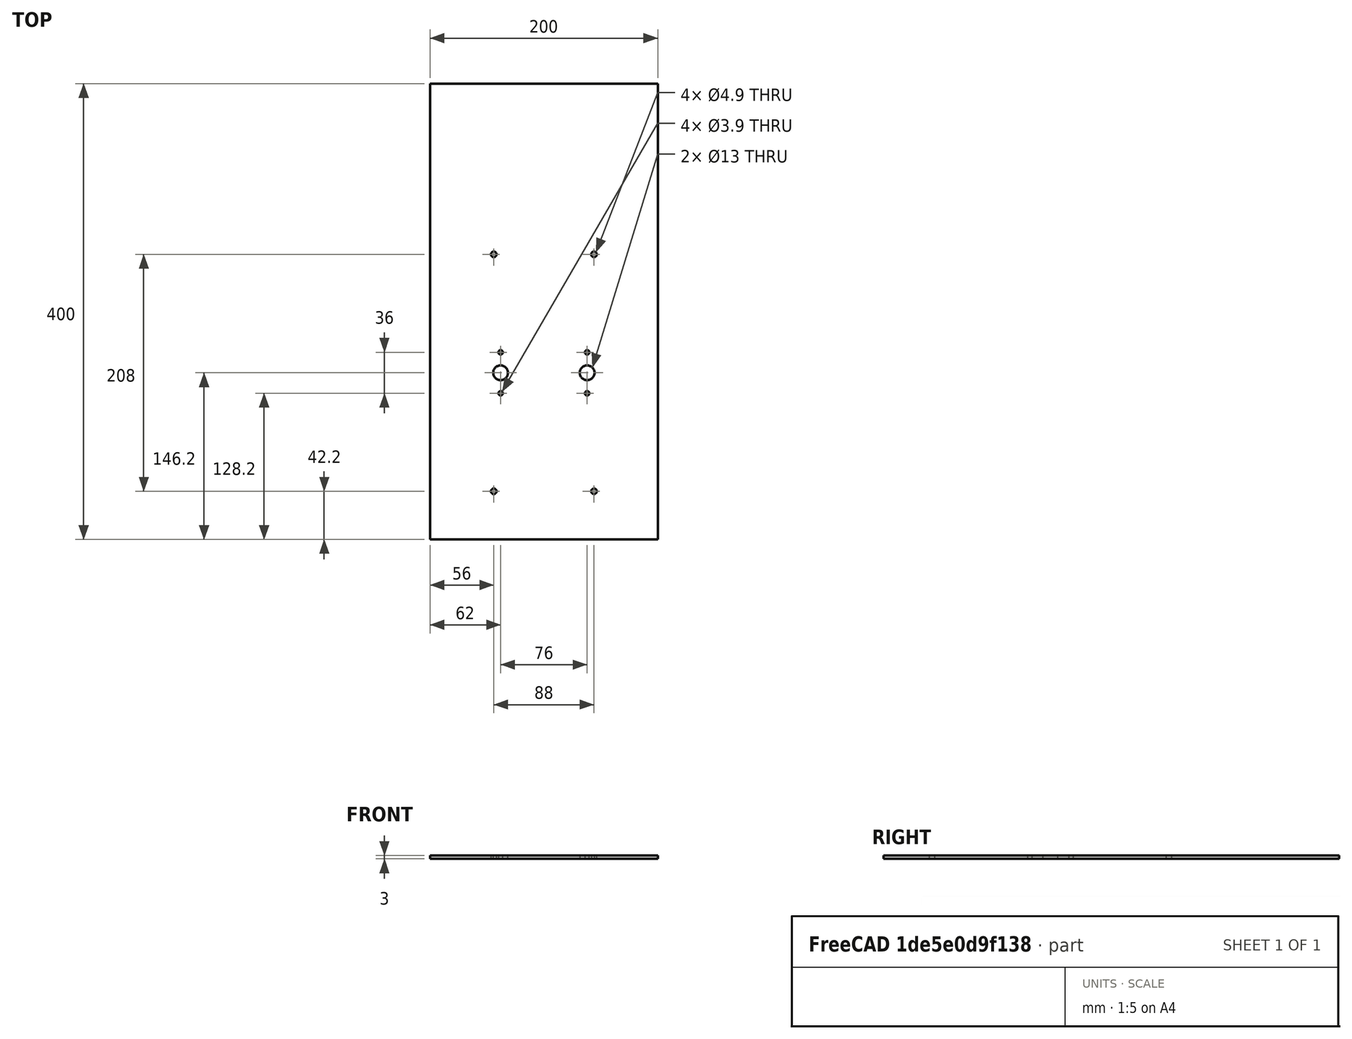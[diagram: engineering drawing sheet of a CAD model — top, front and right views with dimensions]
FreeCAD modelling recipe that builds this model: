
FCSTD DOCUMENT  (FreeCAD 1.0R38641 +468 (Git))
Label: plate_roof
License: All rights reserved
LicenseURL: https://en.wikipedia.org/wiki/All_rights_reserved
objects: TechDraw::DrawViewDimension×10, TechDraw::DrawProjGroupItem×2, Sketcher::SketchObject×1, PartDesign::Pad×1, PartDesign::Body×1, TechDraw::DrawSVGTemplate×1, TechDraw::DrawProjGroup×1, TechDraw::DrawPage×1
note: 22 computed .brp shape members not serialized (recipe doc carries the construction recipe); baked Part::Feature solids carry a one-line shape summary decoded from their .brp

FEATURE [Sketcher::SketchObject] Sketch
  ArcFitTolerance = 1e-06
  AttachmentSupport = -> [XY_Plane]
  FullyConstrained = false
  MakeInternals = false
  MapMode = 5
  sketch-geometry (16):
    g0: LineSegment StartX=-100 StartY=200 StartZ=0 EndX=-100 EndY=-200 EndZ=0
    g1: LineSegment StartX=-100 StartY=-200 StartZ=0 EndX=100 EndY=-200 EndZ=0
    g2: LineSegment StartX=100 StartY=-200 StartZ=0 EndX=100 EndY=200 EndZ=0
    g3: LineSegment StartX=100 StartY=200 StartZ=0 EndX=-100 EndY=200 EndZ=0
    g4: Circle CenterX=-44 CenterY=50.2 CenterZ=0 NormalX=0 NormalY=0 NormalZ=1 AngleXU=0 Radius=2.45
    g5: Circle CenterX=-44 CenterY=-157.8 CenterZ=0 NormalX=0 NormalY=0 NormalZ=1 AngleXU=0 Radius=2.45
    g6: Circle CenterX=44 CenterY=50.2 CenterZ=0 NormalX=0 NormalY=0 NormalZ=1 AngleXU=0 Radius=2.45
    g7: Circle CenterX=44 CenterY=-157.8 CenterZ=0 NormalX=0 NormalY=0 NormalZ=1 AngleXU=0 Radius=2.45
    g8: Circle [constr] CenterX=0 CenterY=0 CenterZ=0 NormalX=0 NormalY=0 NormalZ=1 AngleXU=0 Radius=9.44112
    g9: Circle CenterX=-38 CenterY=-35.8 CenterZ=0 NormalX=0 NormalY=0 NormalZ=1 AngleXU=0 Radius=1.95
    g10: Circle CenterX=-38 CenterY=-71.8 CenterZ=0 NormalX=0 NormalY=0 NormalZ=1 AngleXU=0 Radius=1.95
    g11: Circle CenterX=-38 CenterY=-53.8 CenterZ=0 NormalX=0 NormalY=0 NormalZ=1 AngleXU=0 Radius=6.5
    g12: Circle CenterX=38 CenterY=-35.8 CenterZ=0 NormalX=0 NormalY=0 NormalZ=1 AngleXU=0 Radius=1.95
    g13: Circle CenterX=38 CenterY=-53.8 CenterZ=0 NormalX=0 NormalY=0 NormalZ=1 AngleXU=0 Radius=6.5
    g14: Circle CenterX=38 CenterY=-71.8 CenterZ=0 NormalX=0 NormalY=0 NormalZ=1 AngleXU=0 Radius=1.95
    g15: LineSegment [constr] StartX=0 StartY=0 StartZ=0 EndX=0 EndY=174.663 EndZ=0
  constraints (44):
    c: Coincident(g0,g1)
    c: Coincident(g1,g2)
    c: Coincident(g2,g3)
    c: Coincident(g3,g0)
    c: Vertical(g0)
    c: Vertical(g2)
    c: Horizontal(g1)
    c: Horizontal(g3)
    c: DistanceY(g0,g0) = 400
    c: DistanceX(g3,g3) = 200
    c: Vertical(g4,g5)
    c: Diameter(g4) = 4.9
    c: Equal(g4,g5)
    c: DistanceY(g5,g4) = 208
    c: Horizontal(g6,g4)
    c: Horizontal(g7,g5)
    c: Equal(g6,g4)
    c: Equal(g4,g7)
    c: DistanceX(g4,g6) = 88
    c: Vertical(g7,g6)
    c: DistanceY(g8,g4) = 50.2
    c: DistanceX(g4,g8) = 44
    c: Distance(g8,g3) = 200
    c: Distance(g8,g0) = 100
    c: Vertical(g9,g11)
    c: Vertical(g11,g10)
    c: Vertical(g12,g13)
    c: Vertical(g13,g14)
    c: DistanceY(g11,g9) = 18
    c: DistanceY(g10,g11) = 18
    c: Diameter(g9) = 3.9
    c: Equal(g9,g10)
    c: Equal(g10,g12)
    c: Equal(g12,g14)
    c: Horizontal(g9,g12)
    c: Horizontal(g10,g14)
    c: Equal(g11,g13)
    c: Diameter(g11) = 13
    c: DistanceX(g11,g8) = 38
    c: Horizontal(g11,g13)
    c: DistanceY(g11,g4) = 104
    c: Coincident(g15,g8)
    c: Symmetric(g11,g13,g15)
    c: Coincident(g8,g-1)
FEATURE [PartDesign::Pad] Pad
  Direction = (0,0,1)
  Length = 3
  Length2 = 10
  Profile = -> Sketch
  ReferenceAxis = -> Sketch [N_Axis]
  Refine = true
  Suppressed = false
  Type = 0
FEATURE [PartDesign::Body] Body  label="plate_roof"
  AllowCompound = false
  Group = -> [Sketch,Pad]
  Origin = -> Origin
  Tip = -> Pad
FEATURE [TechDraw::DrawSVGTemplate] Template
  EditableTexts = approval_person=B. Hecate; creator=Djordje Vujic; date_of_issue=20.1.25.; document_type=Assembly Drawing; general_tolerances=ISO 2768-m; identification_number=DN; language_code=EN; part_material=Stainless steel Mat.No. 1.4301; revision_index=AAA; sheet_number=1 / 3; sheet_scale=1 : 2; title=plate_roof
  Height = 297
  Orientation = 0
  Template = /snap/freecad/1248/usr/share/Mod/TechDraw/Templates/A4_Portrait_ISO5457_minimal.svg
  Width = 210
FEATURE [TechDraw::DrawProjGroupItem] ProjItem  label="Front"
  CoarseView = false
  Direction = (0,0,1)
  Focus = 100
  HardHidden = false
  IsoCount = 0
  IsoHidden = false
  IsoVisible = false
  LockPosition = true
  Perspective = false
  Rotation = 0
  RotationVector = (1,0,0)
  Scale = 0.5
  ScaleType = 0
  ScrubCount = 1
  SeamHidden = false
  SeamVisible = false
  SmoothHidden = false
  SmoothVisible = true
  Source = -> [Body]
  Type = 0
  X = 0
  XDirection = (1,0,0)
  Y = 0
FEATURE [TechDraw::DrawProjGroupItem] ProjItem001  label="Bottom"
  CoarseView = false
  Direction = (0,-1,0)
  Focus = 100
  HardHidden = false
  IsoCount = 0
  IsoHidden = false
  IsoVisible = false
  LockPosition = false
  Perspective = false
  Rotation = 0
  RotationVector = (1,0,0)
  Scale = 0.5
  ScaleType = 0
  ScrubCount = 1
  SeamHidden = false
  SeamVisible = false
  SmoothHidden = false
  SmoothVisible = true
  Source = -> [Body]
  Type = 5
  X = 0
  XDirection = (1,0,0)
  Y = 115.75
FEATURE [TechDraw::DrawProjGroup] ProjGroup
  Anchor = -> ProjItem
  AutoDistribute = true
  LockPosition = false
  ProjectionType = 0
  Rotation = 0
  Scale = 0.5
  ScaleType = 2
  Source = -> [Body]
  Views = -> [ProjItem,ProjItem001]
  X = 105
  Y = 162.983
  spacingX = 15
  spacingY = 15
FEATURE [TechDraw::DrawViewDimension] Dimension
  AngleOverride = false
  Arbitrary = false
  ArbitraryTolerances = false
  BoxCorners = (2) [(-50,-0.75,0),(50,0.75,0)]
  EqualTolerance = true
  ExtensionAngle = 0
  FormatSpec = %.2w
  FormatSpecOverTolerance = %+.2w
  FormatSpecUnderTolerance = %+.2w
  Inverted = false
  LineAngle = 0
  LockPosition = false
  MeasureType = 1
  OverTolerance = 0
  References2D = -> [ProjItem001]
  Rotation = 0
  ScaleType = 0
  TheoreticalExact = false
  Type = 2
  UnderTolerance = 0
  X = -62.2509
  Y = -6.95305
FEATURE [TechDraw::DrawViewDimension] Dimension001
  AngleOverride = false
  Arbitrary = false
  ArbitraryTolerances = false
  BoxCorners = (2) [(-50,-0.75,0),(50,0.75,0)]
  EqualTolerance = true
  ExtensionAngle = 0
  FormatSpec = %.2w
  FormatSpecOverTolerance = %+.2w
  FormatSpecUnderTolerance = %+.2w
  Inverted = false
  LineAngle = 0
  LockPosition = false
  MeasureType = 1
  OverTolerance = 0
  References2D = -> [ProjItem001]
  Rotation = 0
  ScaleType = 0
  TheoreticalExact = false
  Type = 1
  UnderTolerance = 0
  X = 0
  Y = -5.41651
FEATURE [TechDraw::DrawViewDimension] Dimension002
  AngleOverride = false
  Arbitrary = false
  ArbitraryTolerances = false
  BoxCorners = (2) [(-50,-100,0),(50,100,0)]
  EqualTolerance = true
  ExtensionAngle = 0
  FormatSpec = %.2w
  FormatSpecOverTolerance = %+.2w
  FormatSpecUnderTolerance = %+.2w
  Inverted = false
  LineAngle = 0
  LockPosition = false
  MeasureType = 1
  OverTolerance = 0
  References2D = -> [ProjItem]
  Rotation = 0
  ScaleType = 0
  TheoreticalExact = false
  Type = 2
  UnderTolerance = 0
  X = -64.6458
  Y = 3.29053
FEATURE [TechDraw::DrawViewDimension] Dimension003
  AngleOverride = false
  Arbitrary = false
  ArbitraryTolerances = false
  BoxCorners = (2) [(-50,-100,0),(50,100,0)]
  EqualTolerance = true
  ExtensionAngle = 0
  FormatSpec = %.2w
  FormatSpecOverTolerance = %+.2w
  FormatSpecUnderTolerance = %+.2w
  Inverted = false
  LineAngle = 0
  LockPosition = false
  MeasureType = 1
  OverTolerance = 0
  References2D = -> [ProjItem]
  Rotation = 0
  ScaleType = 0
  TheoreticalExact = false
  Type = 0
  UnderTolerance = 0
  X = 29.0917
  Y = -31.4
FEATURE [TechDraw::DrawViewDimension] Dimension004
  AngleOverride = false
  Arbitrary = false
  ArbitraryTolerances = false
  BoxCorners = (2) [(-50,-100,0),(50,100,0)]
  EqualTolerance = true
  ExtensionAngle = 0
  FormatSpec = %.2w
  FormatSpecOverTolerance = %+.2w
  FormatSpecUnderTolerance = %+.2w
  Inverted = false
  LineAngle = 0
  LockPosition = false
  MeasureType = 1
  OverTolerance = 0
  References2D = -> [ProjItem]
  Rotation = 0
  ScaleType = 0
  TheoreticalExact = false
  Type = 0
  UnderTolerance = 0
  X = 0
  Y = -5.52183
FEATURE [TechDraw::DrawViewDimension] Dimension005
  AngleOverride = false
  Arbitrary = false
  ArbitraryTolerances = false
  BoxCorners = (2) [(-50,-100,0),(50,100,0)]
  EqualTolerance = true
  ExtensionAngle = 0
  FormatSpec = %.2w
  FormatSpecOverTolerance = %+.2w
  FormatSpecUnderTolerance = %+.2w
  Inverted = false
  LineAngle = 0
  LockPosition = false
  MeasureType = 1
  OverTolerance = 0
  References2D = -> [ProjItem]
  Rotation = 0
  ScaleType = 0
  TheoreticalExact = false
  Type = 0
  UnderTolerance = 0
  X = -34.5
  Y = -5.52183
FEATURE [TechDraw::DrawViewDimension] Dimension006
  AngleOverride = false
  Arbitrary = false
  ArbitraryTolerances = false
  BoxCorners = (2) [(-50,-100,0),(50,100,0)]
  EqualTolerance = true
  ExtensionAngle = 0
  FormatSpec = %.2w
  FormatSpecOverTolerance = %+.2w
  FormatSpecUnderTolerance = %+.2w
  Inverted = false
  LineAngle = 0
  LockPosition = false
  MeasureType = 1
  OverTolerance = 0
  References2D = -> [ProjItem]
  Rotation = 0
  ScaleType = 0
  TheoreticalExact = false
  Type = 0
  UnderTolerance = 0
  X = -33.0527
  Y = -22.4
FEATURE [TechDraw::DrawViewDimension] Dimension007
  AngleOverride = false
  Arbitrary = false
  ArbitraryTolerances = false
  BoxCorners = (2) [(-50,-100,0),(50,100,0)]
  EqualTolerance = false
  ExtensionAngle = 0
  FormatSpec = ⌀%.2w
  FormatSpecOverTolerance = %+.2w
  FormatSpecUnderTolerance = -%.2w
  Inverted = false
  LineAngle = 0
  LockPosition = false
  MeasureType = 1
  OverTolerance = 1
  References2D = -> [ProjItem]
  Rotation = 0
  ScaleType = 0
  TheoreticalExact = false
  Type = 5
  UnderTolerance = 0.9
  X = -9.88409
  Y = -19.3744
FEATURE [TechDraw::DrawViewDimension] Dimension008
  AngleOverride = false
  Arbitrary = false
  ArbitraryTolerances = false
  BoxCorners = (2) [(-50,-100,0),(50,100,0)]
  EqualTolerance = true
  ExtensionAngle = 0
  FormatSpec = %.2w
  FormatSpecOverTolerance = %+.2w
  FormatSpecUnderTolerance = %+.2w
  Inverted = false
  LineAngle = 0
  LockPosition = false
  MeasureType = 1
  OverTolerance = 1
  References2D = -> [ProjItem]
  Rotation = 0
  ScaleType = 0
  TheoreticalExact = false
  Type = 0
  UnderTolerance = -1
  X = 9.62605
  Y = -67.95
FEATURE [TechDraw::DrawViewDimension] Dimension009
  AngleOverride = false
  Arbitrary = false
  ArbitraryTolerances = false
  BoxCorners = (2) [(-50,-100,0),(50,100,0)]
  EqualTolerance = false
  ExtensionAngle = 0
  FormatSpec = ⌀%.2w
  FormatSpecOverTolerance = %+.2w
  FormatSpecUnderTolerance = -%.2w
  Inverted = false
  LineAngle = 0
  LockPosition = false
  MeasureType = 1
  OverTolerance = 0.1
  References2D = -> [ProjItem]
  Rotation = 0
  ScaleType = 0
  TheoreticalExact = false
  Type = 5
  UnderTolerance = 0
  X = -5.75191
  Y = -38.5146
FEATURE [TechDraw::DrawPage] Page
  KeepUpdated = true
  NextBalloonIndex = 1
  ProjectionType = 0
  Template = -> Template
  Views = -> [ProjGroup,Dimension,Dimension001,Dimension002,Dimension003,Dimension004,Dimension005,Dimension006,Dimension007,Dimension008,Dimension009]
